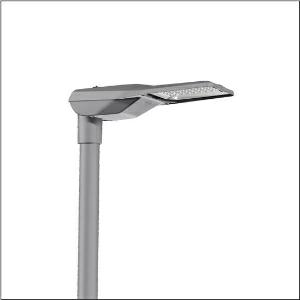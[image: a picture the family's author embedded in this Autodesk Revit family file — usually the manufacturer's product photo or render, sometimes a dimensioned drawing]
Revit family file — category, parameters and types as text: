
# Revit family: streetlight_sl_21_iq_mini___st1_0ab_5xe2m31v08hb_1211
name_source: partatom
category: Lighting Fixtures
units: mm (PartAtom-declared; Revit-internal decimal feet)

## family parameters
Cut with Voids When Loaded = No
Host = Face
Light Source = No
Part Type = Normal
Room Calculation Point = No
Round Connector Dimension = Use Diameter
Shared = No

## types (1)
- --- (1 x LED, 8580 lm, 71 W, 3000K)
    Apparent Load = 71 VA
    CIE Flux Codes = 38 73 97 100 100
    Color Rendering = 70
    Color Temperature = 3000K
    Default Elevation = 1800 mm
    Description = Streetlight SL 21 iQ mini, mast luminaire, primary light control with lens, of PMMA, primary optical cover: cover, of toughened safety glass, transparent, light distribution: ST1.0aB, light emission: direct distribution, primary light characteristic: asymmetric, installation type: post-top, side-entry, LED, High Power LED, rated luminous flux: 8.580lm, luminous efficacy: 121lm/W, light colour: 730, colour temperature: 3000K, control gear: iQ-Street Remote, D4i with power reduction, control: pre-setting: logarithmic dimming characteristic, Street-Remote, Auto-Match, Temp-Guard, Lumen-Switch, Night-Set, Smart-Wire, Light-Fading, Desk-Remote (wireless, voltage-free reading and setting of iQ features in the workshop via application-optimized NFC function/RFID function), optimised constant luminous flux control (CLO 2.0), mains connection: 220..240V, AC, 50/60Hz, start of lifetime: 71W, end of service life: 75W, reduction: 30W, luminaire housing, of diecast aluminium, powder-coated, SITECO metallic grey (DB 702S), corrosivity category C5 high according to DIN EN ISO 12944, please order mast flange separately, inclination adjustable: 0°, 5°, 10°, 15°, sealing non-destructively replaceable, multi-level sealing system, length: 628mm, width: 235mm, height: 110mm, mast flange for spigot size: 42mm (side-entry): 5XC10008XM4, 60/48mm (side-entry/post-top): 5XC10108XM2, 76/60mm (side-entry/post-top): 5XC10108XM1, mounting height: 4..8m, Smart Interface above, protection rating (complete): IP66, insulation class (complete): insulation class II (safety insulation), certification: CE, ENEC, ENEC+, VDE, impact resistance: IK10, permissible operating ambient temperature for outdoor applications: -40..+50°C, standard-compliant lighting for roads and squares, packaging unit: 1 piece

Light Distribution: ST1.0aB
    Height = 110 mm
    Lamp = 1 x LED
    Lamp Light Flux = 8580 lm
    Lamp Power = 71 W
    Lamp count = 1
    Length = 625 mm
    Luminous efficacy = 121 lm/W
    Manufacturer = Siteco
    ModVariant = No
    Model = 5XE2M31V08HB
    Mounting Place = Pole
    Mounting Type = Pole top
    Number of Poles = 1
    OnlyDefault = Yes
    Power Factor = 1
    Product Name = Streetlight SL 21 iQ mini | ST1.0aB
    Product group = mast luminaire | pylon top
    ProductGroupID = 6100
    Protection Class = Protection class II
    Protection Degree = IP 66
    RLX_Detail_Level = 1
    RLX_Emergency_Light_Flux = 0 lm
    RLX_Emergency_Type = 0
    RLX_Emergency_Type_DB = No
    RlxData = <blob elided: 92413 chars, md5=ffef9229>
    Socket = socket
    Standby Power = 0 W
    System Light Flux = 8580 lm
    System Power = 71 W
    Type Comments = factory setting: luminous flux: 100 % | dim-lin: 254 | 716 mA
    Type Image = l_1003515.jpg
    URL = http://relux.com
    VarID = @adj_114025
    Voltage = 0 V
    Weight = 0.00 kg
    Width = 234 mm

## geometry (parser evidence)
native form markers: Blend x4, Sweep x12
no freeform markers — native parametric forms only
